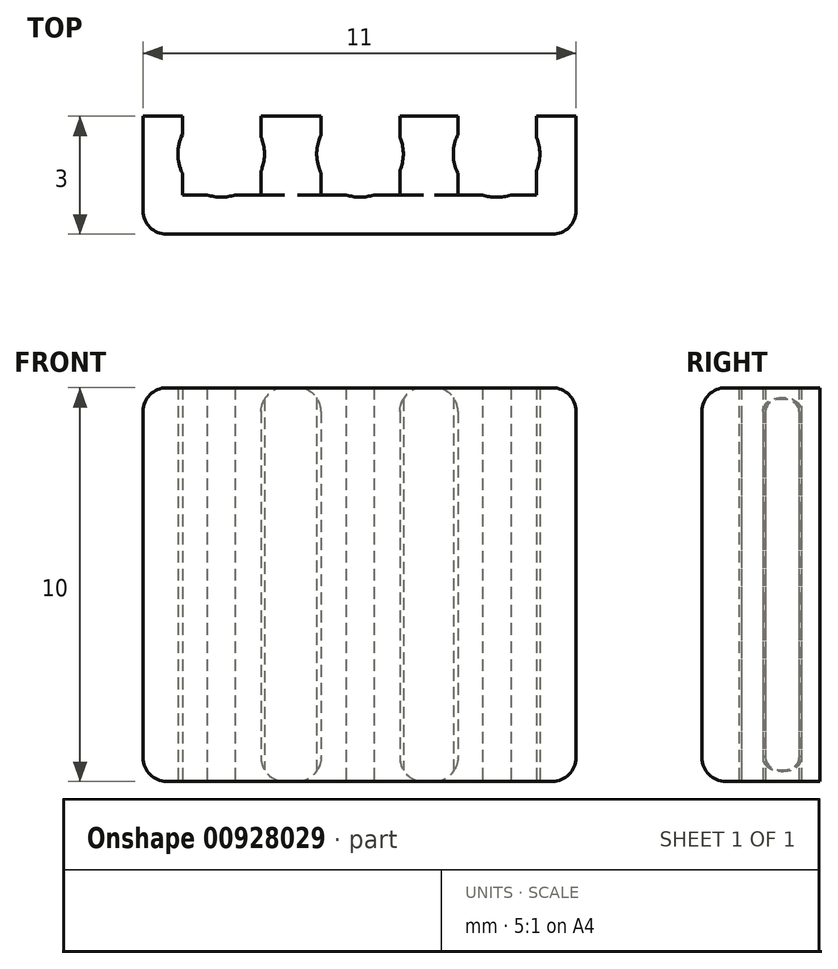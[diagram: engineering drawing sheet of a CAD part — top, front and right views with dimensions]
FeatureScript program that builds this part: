
annotation { "Feature Type Name" : "Feature", "Feature Type Description" : "" }
export const myFeature = defineFeature(function(context is Context, id is Id, definition is map)
    precondition{}
    {
        {
            var Q0;
            Q0=qCreatedBy(makeId("Front.planeOp"),FACE);
            var sketch = newSketch(context, id + "F0", { "sketchPlane" : qUnion([Q0])});
            skArc(sketch, "E0", {"start": v(-58.35, 29.44) * mm, "mid": v(-57.2, 28.65) * mm, "end": v(-56.38, 29.8) * mm});
            skArc(sketch, "E1", {"start": v(-52.86, 28.84) * mm, "mid": v(-49.52, 27.34) * mm, "end": v(-50.66, 30.82) * mm});
            skLineSegment(sketch, "E2.bottom", {"start": v(-46.54, 29.63) * mm, "end": v(-35.54, 29.63) * mm});
            skLineSegment(sketch, "E2.top", {"start": v(-46.54, 19.63) * mm, "end": v(-35.54, 19.63) * mm});
            skLineSegment(sketch, "E2.left", {"start": v(-46.54, 29.63) * mm, "end": v(-46.54, 19.63) * mm});
            skLineSegment(sketch, "E2.right", {"start": v(-35.54, 29.63) * mm, "end": v(-35.54, 19.63) * mm});
            skLineSegment(sketch, "E3.bottom", {"start": v(-45.54, 29.63) * mm, "end": v(-43.54, 29.63) * mm});
            skLineSegment(sketch, "E3.top", {"start": v(-45.54, 19.63) * mm, "end": v(-43.54, 19.63) * mm});
            skLineSegment(sketch, "E3.left", {"start": v(-45.54, 29.63) * mm, "end": v(-45.54, 19.63) * mm});
            skLineSegment(sketch, "E3.right", {"start": v(-43.54, 29.63) * mm, "end": v(-43.54, 19.63) * mm});
            skLineSegment(sketch, "E4.bottom", {"start": v(-42.02, 29.63) * mm, "end": v(-40.02, 29.63) * mm});
            skLineSegment(sketch, "E4.top", {"start": v(-42.02, 19.63) * mm, "end": v(-40.02, 19.63) * mm});
            skLineSegment(sketch, "E4.left", {"start": v(-42.02, 29.63) * mm, "end": v(-42.02, 19.63) * mm});
            skLineSegment(sketch, "E4.right", {"start": v(-40.02, 29.63) * mm, "end": v(-40.02, 19.63) * mm});
            skLineSegment(sketch, "E5.bottom", {"start": v(-38.54, 29.63) * mm, "end": v(-36.54, 29.63) * mm});
            skLineSegment(sketch, "E5.top", {"start": v(-38.54, 19.63) * mm, "end": v(-36.54, 19.63) * mm});
            skLineSegment(sketch, "E5.left", {"start": v(-38.54, 29.63) * mm, "end": v(-38.54, 19.63) * mm});
            skLineSegment(sketch, "E5.right", {"start": v(-36.54, 29.63) * mm, "end": v(-36.54, 19.63) * mm});
            skSolve(sketch);
        }
        {
            var Q0;
            {var subQ0=sQuery(id+"F0.wireOp",EDGE,"E2.left");Q0=makeQuery(id+"F0.imprint","IMPRINT",FACE,{"disambiguationData":[TD([[makeQuery(id+"F0.imprint","IMPRINT",EDGE,{"derivedFrom":subQ0}),1.0]])]});}
            var Q1;
            {var subQ0=sQuery(id+"F0.wireOp",EDGE,"E3.right");Q1=makeQuery(id+"F0.imprint","IMPRINT",FACE,{"disambiguationData":[TD([[makeQuery(id+"F0.imprint","IMPRINT",EDGE,{"derivedFrom":subQ0}),1.0]])]});}
            var Q2;
            {var subQ2=sQuery(id+"F0.wireOp",EDGE,"E4.right");Q2=makeQuery(id+"F0.imprint","IMPRINT",FACE,{"disambiguationData":[TD([[makeQuery(id+"F0.imprint","IMPRINT",EDGE,{"derivedFrom":subQ2}),1.0]])]});}
            var Q3;
            {var subQ0=sQuery(id+"F0.wireOp",EDGE,"E2.right");Q3=makeQuery(id+"F0.imprint","IMPRINT",FACE,{"disambiguationData":[TD([[makeQuery(id+"F0.imprint","IMPRINT",EDGE,{"derivedFrom":subQ0}),-1.0]])]});}
            extrude(context, id + "F1", {"entities" : qUnion([Q0, Q1, Q2, Q3]), "oppositeDirection" : true, "depth" : 2 * mm, "offsetDistance" : 25 * mm});
        }
        {
            var Q0;
            {var subQ0=sQuery(id+"F0.wireOp",EDGE,"E5.left");var subQ5=makeQuery(id+"F0.imprint","IMPRINT",EDGE,{"derivedFrom":subQ0});var subQ10=sQuery(id+"F0.wireOp",EDGE,"E3.right");var subQ12=sQuery(id+"F0.wireOp",EDGE,"E4.left");var subQ14=makeQuery(id+"F0.imprint","IMPRINT",EDGE,{"derivedFrom":subQ12});var subQ17=makeQuery(id+"F0.imprint","IMPRINT",EDGE,{"derivedFrom":subQ10});var subQ18=sQuery(id+"F0.wireOp",EDGE,"E2.right");var subQ19=sQuery(id+"F0.wireOp",EDGE,"E3.left");var subQ22=makeQuery(id+"F0.imprint","IMPRINT",EDGE,{"derivedFrom":subQ19});var subQ23=sQuery(id+"F0.wireOp",EDGE,"E2.left");var subQ24=sQuery(id+"F0.wireOp",EDGE,"E4.right");var subQ26=makeQuery(id+"F0.imprint","IMPRINT",EDGE,{"derivedFrom":subQ24});Q0=qUnion([makeQuery(id+"F0.imprint","IMPRINT",FACE,{"disambiguationData":[TD([[subQ14,1.0]])]}),makeQuery(id+"F0.imprint","IMPRINT",FACE,{"disambiguationData":[TD([[subQ26,1.0]])]}),makeQuery(id+"F0.imprint","IMPRINT",FACE,{"disambiguationData":[TD([[makeQuery(id+"F0.imprint","IMPRINT",EDGE,{"derivedFrom":subQ23}),1.0]])]}),makeQuery(id+"F0.imprint","IMPRINT",FACE,{"disambiguationData":[TD([[subQ22,1.0]])]}),makeQuery(id+"F0.imprint","IMPRINT",FACE,{"disambiguationData":[TD([[makeQuery(id+"F0.imprint","IMPRINT",EDGE,{"derivedFrom":subQ18}),-1.0]])]}),makeQuery(id+"F0.imprint","IMPRINT",FACE,{"disambiguationData":[TD([[subQ17,1.0]])]}),makeQuery(id+"F0.imprint","IMPRINT",FACE,{"disambiguationData":[TD([[subQ5,1.0]])]})]);}
            var Q1;
            {var subQ0=sQuery(id+"F0.wireOp",EDGE,"E2.left");Q1=makeQuery(id+"F0.imprint","IMPRINT",FACE,{"disambiguationData":[TD([[makeQuery(id+"F0.imprint","IMPRINT",EDGE,{"derivedFrom":subQ0}),1.0]])]});}
            var Q2;
            {var subQ0=sQuery(id+"F0.wireOp",EDGE,"E3.left");Q2=makeQuery(id+"F0.imprint","IMPRINT",FACE,{"disambiguationData":[TD([[makeQuery(id+"F0.imprint","IMPRINT",EDGE,{"derivedFrom":subQ0}),1.0]])]});}
            var Q3;
            {var subQ0=sQuery(id+"F0.wireOp",EDGE,"E3.right");Q3=makeQuery(id+"F0.imprint","IMPRINT",FACE,{"disambiguationData":[TD([[makeQuery(id+"F0.imprint","IMPRINT",EDGE,{"derivedFrom":subQ0}),1.0]])]});}
            var Q4;
            {var subQ0=sQuery(id+"F0.wireOp",EDGE,"E4.left");Q4=makeQuery(id+"F0.imprint","IMPRINT",FACE,{"disambiguationData":[TD([[makeQuery(id+"F0.imprint","IMPRINT",EDGE,{"derivedFrom":subQ0}),1.0]])]});}
            var Q5;
            {var subQ2=sQuery(id+"F0.wireOp",EDGE,"E4.right");Q5=makeQuery(id+"F0.imprint","IMPRINT",FACE,{"disambiguationData":[TD([[makeQuery(id+"F0.imprint","IMPRINT",EDGE,{"derivedFrom":subQ2}),1.0]])]});}
            var Q6;
            {var subQ0=sQuery(id+"F0.wireOp",EDGE,"E5.left");Q6=makeQuery(id+"F0.imprint","IMPRINT",FACE,{"disambiguationData":[TD([[makeQuery(id+"F0.imprint","IMPRINT",EDGE,{"derivedFrom":subQ0}),1.0]])]});}
            var Q7;
            {var subQ0=sQuery(id+"F0.wireOp",EDGE,"E2.right");Q7=makeQuery(id+"F0.imprint","IMPRINT",FACE,{"disambiguationData":[TD([[makeQuery(id+"F0.imprint","IMPRINT",EDGE,{"derivedFrom":subQ0}),-1.0]])]});}
            extrude(context, id + "F2", {"entities" : qUnion([Q0, Q1, Q2, Q3, Q4, Q5, Q6, Q7]), "operationType" : NewBodyOperationType.ADD, "depth" : 1 * mm, "offsetDistance" : 25 * mm});
        }
        {
            var Q0;
            Q0=makeQuery(id+"F1.opExtrude","SWEPT_EDGE",EDGE,{"disambiguationData":[OSD([sQuery(id+"F0.wireOp",EDGE,"E2.bottom"),sQuery(id+"F0.wireOp",EDGE,"E3.right")])]});
            var Q1;
            Q1=makeQuery(id+"F1.opExtrude","SWEPT_EDGE",EDGE,{"disambiguationData":[OSD([sQuery(id+"F0.wireOp",EDGE,"E2.bottom"),sQuery(id+"F0.wireOp",EDGE,"E4.left")])]});
            var Q2;
            Q2=makeQuery(id+"F1.opExtrude","SWEPT_EDGE",EDGE,{"disambiguationData":[OSD([sQuery(id+"F0.wireOp",EDGE,"E2.top"),sQuery(id+"F0.wireOp",EDGE,"E4.right")])]});
            var Q3;
            Q3=makeQuery(id+"F1.opExtrude","SWEPT_EDGE",EDGE,{"disambiguationData":[OSD([sQuery(id+"F0.wireOp",EDGE,"E2.top"),sQuery(id+"F0.wireOp",EDGE,"E5.left")])]});
            var Q4;
            Q4=makeQuery(id+"F1.opExtrude","SWEPT_EDGE",EDGE,{"disambiguationData":[OSD([sQuery(id+"F0.wireOp",EDGE,"E2.bottom"),sQuery(id+"F0.wireOp",EDGE,"E4.right")])]});
            var Q5;
            Q5=makeQuery(id+"F1.opExtrude","SWEPT_EDGE",EDGE,{"disambiguationData":[OSD([sQuery(id+"F0.wireOp",EDGE,"E2.bottom"),sQuery(id+"F0.wireOp",EDGE,"E5.left")])]});
            var Q6;
            Q6=makeQuery(id+"F1.opExtrude","SWEPT_EDGE",EDGE,{"disambiguationData":[OSD([sQuery(id+"F0.wireOp",EDGE,"E2.top"),sQuery(id+"F0.wireOp",EDGE,"E3.right")])]});
            var Q7;
            Q7=makeQuery(id+"F1.opExtrude","SWEPT_EDGE",EDGE,{"disambiguationData":[OSD([sQuery(id+"F0.wireOp",EDGE,"E2.top"),sQuery(id+"F0.wireOp",EDGE,"E4.left")])]});
            var Q8;
            {var subQ0=sQuery(id+"F0.wireOp",EDGE,"E2.left");var subQ1=sQuery(id+"F0.wireOp",EDGE,"E2.top");Q8=makeQuery(id+"F2.boolean.opBoolean","MERGE",EDGE,{"derivedFrom":[makeQuery(id+"F1.opExtrude","SWEPT_EDGE",EDGE,{"disambiguationData":[OSD([subQ1,subQ0])]}),makeQuery(id+"F2.opExtrude","SWEPT_EDGE",EDGE,{"disambiguationData":[OSD([subQ1,subQ0])]})]});}
            var Q9;
            {var subQ0=sQuery(id+"F0.wireOp",EDGE,"E2.left");var subQ1=sQuery(id+"F0.wireOp",EDGE,"E2.bottom");Q9=makeQuery(id+"F2.boolean.opBoolean","MERGE",EDGE,{"derivedFrom":[makeQuery(id+"F1.opExtrude","SWEPT_EDGE",EDGE,{"disambiguationData":[OSD([subQ1,subQ0])]}),makeQuery(id+"F2.opExtrude","SWEPT_EDGE",EDGE,{"disambiguationData":[OSD([subQ1,subQ0])]})]});}
            var Q10;
            {var subQ0=sQuery(id+"F0.wireOp",EDGE,"E2.right");var subQ1=sQuery(id+"F0.wireOp",EDGE,"E2.bottom");Q10=makeQuery(id+"F2.boolean.opBoolean","MERGE",EDGE,{"derivedFrom":[makeQuery(id+"F1.opExtrude","SWEPT_EDGE",EDGE,{"disambiguationData":[OSD([subQ1,subQ0])]}),makeQuery(id+"F2.opExtrude","SWEPT_EDGE",EDGE,{"disambiguationData":[OSD([subQ1,subQ0])]})]});}
            var Q11;
            Q11=makeQuery(id+"F2.opExtrude","CAP_EDGE",EDGE,{"disambiguationData":[OSD([sQuery(id+"F0.wireOp",EDGE,"E2.bottom")])],"isStart":false});
            var Q12;
            Q12=makeQuery(id+"F2.opExtrude","CAP_EDGE",EDGE,{"disambiguationData":[OSD([sQuery(id+"F0.wireOp",EDGE,"E2.right")])],"isStart":false});
            var Q13;
            Q13=makeQuery(id+"F2.opExtrude","CAP_EDGE",EDGE,{"disambiguationData":[OSD([sQuery(id+"F0.wireOp",EDGE,"E2.left")])],"isStart":false});
            var Q14;
            Q14=makeQuery(id+"F2.opExtrude","CAP_EDGE",EDGE,{"disambiguationData":[OSD([sQuery(id+"F0.wireOp",EDGE,"E2.top")])],"isStart":false});
            var Q15;
            {var subQ0=sQuery(id+"F0.wireOp",EDGE,"E2.right");var subQ1=sQuery(id+"F0.wireOp",EDGE,"E2.top");Q15=makeQuery(id+"F2.boolean.opBoolean","MERGE",EDGE,{"derivedFrom":[makeQuery(id+"F1.opExtrude","SWEPT_EDGE",EDGE,{"disambiguationData":[OSD([subQ1,subQ0])]}),makeQuery(id+"F2.opExtrude","SWEPT_EDGE",EDGE,{"disambiguationData":[OSD([subQ1,subQ0])]})]});}
            fillet(context, id + "F3", {"entities" : qUnion([Q0, Q1, Q2, Q3, Q4, Q5, Q6, Q7, Q8, Q9, Q10, Q11, Q12, Q13, Q14, Q15]), "radius" : .6 * mm, "tangentPropagation" : true, "allowEdgeOverflow" : false});
        }
        {
            var Q0;
            Q0=qCreatedBy(makeId("Top.planeOp"),FACE);
            var sketch = newSketch(context, id + "F4", { "sketchPlane" : qUnion([Q0])});
            skCircle(sketch, "E6", {"center": v(-37.56, 1.04) * mm, "radius": 1.1 * mm});
            skCircle(sketch, "E7", {"center": v(-41.03, 1.04) * mm, "radius": 1.1 * mm});
            skCircle(sketch, "E8", {"center": v(-44.56, 1.04) * mm, "radius": 1.1 * mm});
            skSolve(sketch);
        }
        {
            var Q0;
            Q0=makeQuery(id+"F4.imprint","IMPRINT",FACE,{"disambiguationData":[TD([[makeQuery(id+"F4.imprint","IMPRINT",EDGE,{"derivedFrom":sQuery(id+"F4.wireOp",EDGE,"E6")}),1.0]])]});
            var Q1;
            Q1=makeQuery(id+"F4.imprint","IMPRINT",FACE,{"disambiguationData":[TD([[makeQuery(id+"F4.imprint","IMPRINT",EDGE,{"derivedFrom":sQuery(id+"F4.wireOp",EDGE,"E7")}),1.0]])]});
            var Q2;
            Q2=makeQuery(id+"F4.imprint","IMPRINT",FACE,{"disambiguationData":[TD([[makeQuery(id+"F4.imprint","IMPRINT",EDGE,{"derivedFrom":sQuery(id+"F4.wireOp",EDGE,"E8")}),1.0]])]});
            extrude(context, id + "F5", {"entities" : qUnion([Q0, Q1, Q2]), "operationType" : NewBodyOperationType.REMOVE, "depth" : 50 * mm, "offsetDistance" : 25 * mm});
        }
    });
